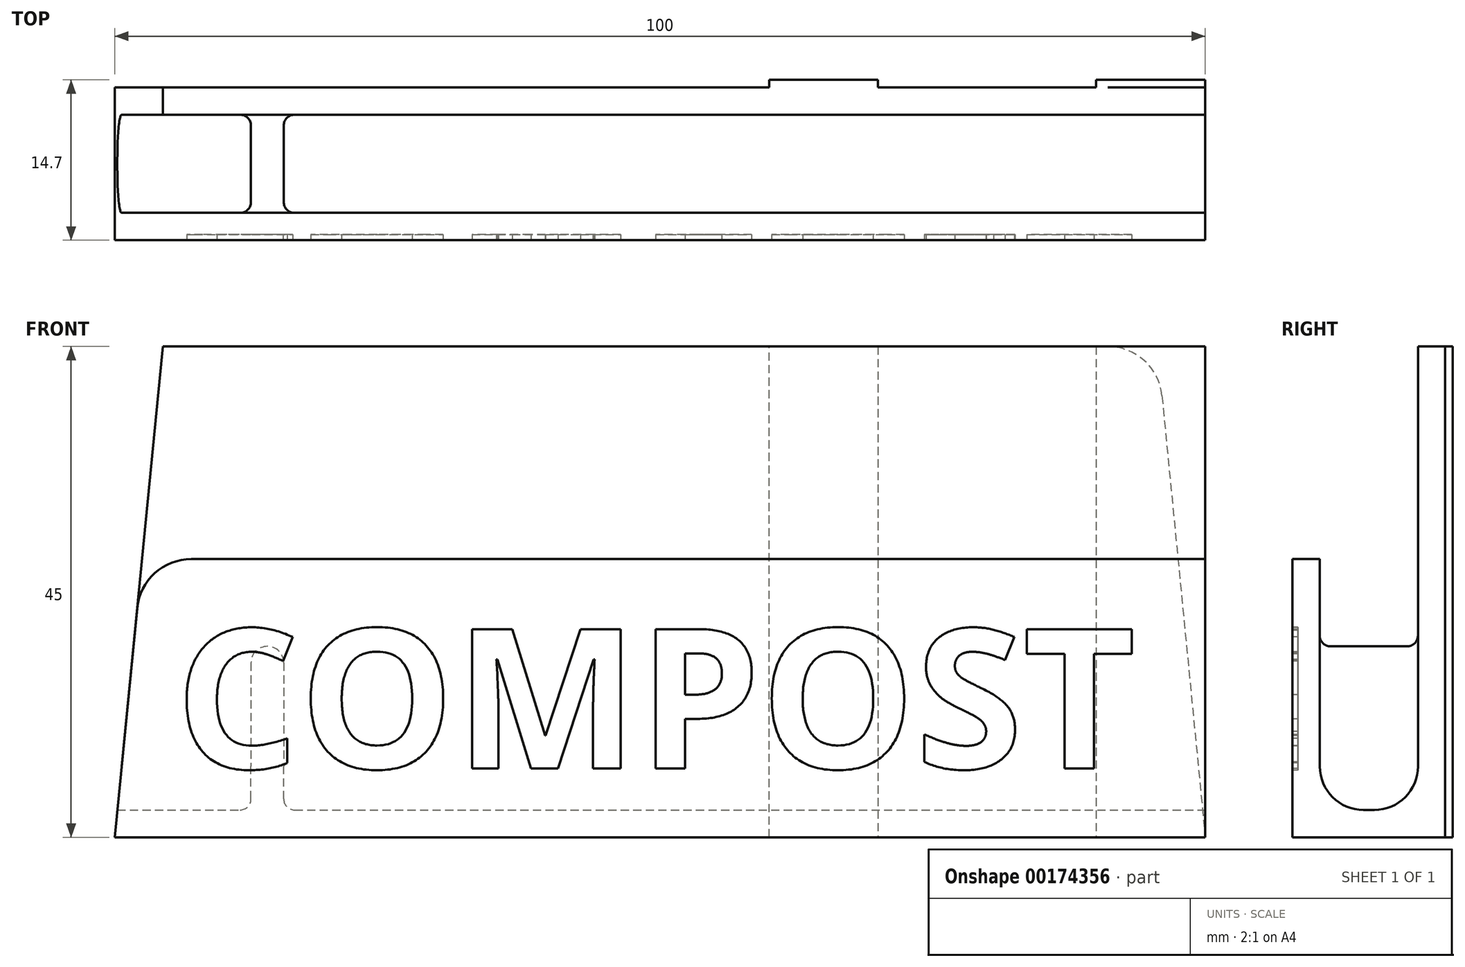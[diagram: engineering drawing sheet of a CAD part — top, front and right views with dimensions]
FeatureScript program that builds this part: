
annotation { "Feature Type Name" : "Feature", "Feature Type Description" : "" }
export const myFeature = defineFeature(function(context is Context, id is Id, definition is map)
    precondition{}
    {
        {
            var Q0;
            Q0=qCreatedBy(makeId("Top.planeOp"),FACE);
            var sketch = newSketch(context, id + "F0", { "sketchPlane" : qUnion([Q0])});
            skLineSegment(sketch, "E0.bottom", {"start": v(-50, 0) * mm, "end": v(50, 0) * mm});
            skLineSegment(sketch, "E0.top", {"start": v(-50, -14) * mm, "end": v(50, -14) * mm});
            skLineSegment(sketch, "E0.left", {"start": v(-50, 0) * mm, "end": v(-50, -14) * mm});
            skLineSegment(sketch, "E0.right", {"start": v(50, 0) * mm, "end": v(50, -14) * mm});
            skSolve(sketch);
        }
        {
            var Q0;
            Q0 = qSketchRegion(id + "F0", true);
            extrude(context, id + "F1", {"entities" : qUnion([Q0]), "depth" : 45 * mm});
        }
        {
            var Q0;
            Q0=makeQuery(id+"F1.opExtrude","CAP_FACE",FACE,{"disambiguationData":[OSD([sQuery(id+"F0.wireOp",EDGE,"E0.bottom"),sQuery(id+"F0.wireOp",EDGE,"E0.top"),sQuery(id+"F0.wireOp",EDGE,"E0.left"),sQuery(id+"F0.wireOp",EDGE,"E0.right")])],"isStart":false});
            var Q1;
            Q1=makeQuery(id+"F1.opExtrude","SWEPT_FACE",FACE,{"disambiguationData":[OSD([sQuery(id+"F0.wireOp",EDGE,"E0.left")])]});
            var Q2;
            Q2=makeQuery(id+"F1.opExtrude","SWEPT_FACE",FACE,{"disambiguationData":[OSD([sQuery(id+"F0.wireOp",EDGE,"E0.right")])]});
            shell(context, id + "F2", {"entities" : qUnion([Q0, Q1, Q2]), "thickness" : 2.5 * mm});
        }
        {
            var Q0;
            Q0=makeQuery(id+"F1.opExtrude","SWEPT_FACE",FACE,{"disambiguationData":[OSD([sQuery(id+"F0.wireOp",EDGE,"E0.top")])]});
            var sketch = newSketch(context, id + "F3", { "sketchPlane" : qUnion([Q0])});
            skLineSegment(sketch, "E1.bottom", {"start": v(-50, 45) * mm, "end": v(50, 45) * mm});
            skLineSegment(sketch, "E1.top", {"start": v(-50, 25.5) * mm, "end": v(50, 25.5) * mm});
            skLineSegment(sketch, "E1.left", {"start": v(-50, 45) * mm, "end": v(-50, 25.5) * mm});
            skLineSegment(sketch, "E1.right", {"start": v(50, 45) * mm, "end": v(50, 25.5) * mm});
            skLineSegment(sketch, "E2.0", {"start": v(-50, 2.5) * mm, "end": v(50, 2.5) * mm, "construction": true});
            skSolve(sketch);
        }
        {
            var Q0;
            Q0 = qSketchRegion(id + "F3", true);
            extrude(context, id + "F4", {"entities" : qUnion([Q0]), "operationType" : NewBodyOperationType.REMOVE, "endBound" : BoundingType.UP_TO_NEXT, "oppositeDirection" : true, "depth" : 25 * mm});
        }
        {
            var Q0;
            Q0=qCreatedBy(makeId("Front.planeOp"),FACE);
            var sketch = newSketch(context, id + "F5", { "sketchPlane" : qUnion([Q0])});
            skLineSegment(sketch, "E3", {"start": v(-45.59, 45) * mm, "end": v(-50, 0) * mm});
            skLineSegment(sketch, "E4", {"start": v(-50, 0) * mm, "end": v(-50, 45) * mm});
            skLineSegment(sketch, "E5", {"start": v(-50, 45) * mm, "end": v(-45.59, 45) * mm});
            skLineSegment(sketch, "E6", {"start": v(0, 0) * mm, "end": v(0, 36.7) * mm, "construction": true});
            skPoint(sketch, "E7", {"position": v(-47.5, 25.5) * mm});
            skSolve(sketch);
        }
        {
            var Q0;
            Q0 = qSketchRegion(id + "F5", true);
            extrude(context, id + "F6", {"entities" : qUnion([Q0]), "operationType" : NewBodyOperationType.REMOVE, "endBound" : BoundingType.THROUGH_ALL, "depth" : 25 * mm});
        }
        {
            var Q0;
            Q0=qCreatedBy(makeId("Front.planeOp"),FACE);
            var sketch = newSketch(context, id + "F7", { "sketchPlane" : qUnion([Q0])});
            skLineSegment(sketch, "E8.0", {"start": v(-55.05, 2.5) * mm, "end": v(50, 2.5) * mm, "construction": true});
            skLineSegment(sketch, "E9", {"start": v(-37.5, 2.5) * mm, "end": v(-37.5, 16) * mm});
            skArc(sketch, "E10", {"start": v(-34.5, 16) * mm, "mid": v(-36, 17.5) * mm, "end": v(-37.5, 16) * mm});
            skLineSegment(sketch, "E11", {"start": v(-34.5, 16) * mm, "end": v(-34.5, 2.5) * mm});
            skLineSegment(sketch, "E12", {"start": v(-36, 17.5) * mm, "end": v(-31.62, 17.5) * mm, "construction": true});
            skLineSegment(sketch, "E13", {"start": v(0, 0) * mm, "end": v(0, 34.62) * mm, "construction": true});
            skLineSegment(sketch, "E14", {"start": v(-37.5, 2.5) * mm, "end": v(-34.5, 2.5) * mm});
            skSolve(sketch);
        }
        {
            var Q0;
            Q0 = qSketchRegion(id + "F7", true);
            var Q1;
            Q1=makeQuery(id+"F2.opShell","OFFSET_FACE",FACE,{"disambiguationData":[OSD([sQuery(id+"F0.wireOp",EDGE,"E0.top")])]});
            extrude(context, id + "F8", {"entities" : qUnion([Q0]), "operationType" : NewBodyOperationType.ADD, "endBound" : BoundingType.UP_TO_SURFACE, "endBoundEntityFace" : qUnion([Q1]), "depth" : 25 * mm});
        }
        {
            var Q0;
            {var subQ0=sQuery(id+"F0.wireOp",EDGE,"E0.bottom");var subQ2=sQuery(id+"F0.wireOp",EDGE,"E0.right");var subQ6=sQuery(id+"F7.wireOp",EDGE,"E11");var subQ7=makeQuery(id+"F8.opExtrude","SWEPT_FACE",FACE,{"disambiguationData":[OSD([subQ6])]});Q0=makeQuery(id+"F897hcUD9pJ6nv1_1.1.F8.boolean.opBoolean","SPLIT",EDGE,{"disambiguationData":[TD([subQ7])],"derivedFrom":makeQuery(id+"F8.boolean.opBoolean","SPLIT",EDGE,{"disambiguationData":[TD([makeQuery(id+"F1.opExtrude","SWEPT_FACE",FACE,{"disambiguationData":[OSD([subQ2])]})])],"derivedFrom":makeQuery(id+"F2.opShell","OFFSET_EDGE",EDGE,{"disambiguationData":[OSD([subQ0]),TDD([makeQuery(id+"F1.opExtrude","CAP_EDGE",EDGE,{"disambiguationData":[OSD([subQ0])],"isStart":true})])]})})});}
            var Q1;
            {var subQ0=sQuery(id+"F0.wireOp",EDGE,"E0.left");var subQ1=sQuery(id+"F0.wireOp",EDGE,"E0.bottom");Q1=makeQuery(id+"F8.boolean.opBoolean","SPLIT",EDGE,{"disambiguationData":[TD([makeQuery(id+"F1.opExtrude","SWEPT_FACE",FACE,{"disambiguationData":[OSD([subQ0])]})])],"derivedFrom":makeQuery(id+"F2.opShell","OFFSET_EDGE",EDGE,{"disambiguationData":[OSD([subQ1]),TDD([makeQuery(id+"F1.opExtrude","CAP_EDGE",EDGE,{"disambiguationData":[OSD([subQ1])],"isStart":true})])]})});}
            var Q2;
            {var subQ0=sQuery(id+"F0.wireOp",EDGE,"E0.right");var subQ1=makeQuery(id+"F1.opExtrude","SWEPT_FACE",FACE,{"disambiguationData":[OSD([subQ0])]});var subQ2=sQuery(id+"F0.wireOp",EDGE,"E0.bottom");Q2=makeQuery(id+"F897hcUD9pJ6nv1_1.1.F8.boolean.opBoolean","SPLIT",EDGE,{"disambiguationData":[TD([subQ1])],"derivedFrom":makeQuery(id+"F8.boolean.opBoolean","SPLIT",EDGE,{"disambiguationData":[TD([subQ1])],"derivedFrom":makeQuery(id+"F2.opShell","OFFSET_EDGE",EDGE,{"disambiguationData":[OSD([subQ2]),TDD([makeQuery(id+"F1.opExtrude","CAP_EDGE",EDGE,{"disambiguationData":[OSD([subQ2])],"isStart":true})])]})})});}
            var Q3;
            {var subQ0=sQuery(id+"F0.wireOp",EDGE,"E0.right");var subQ1=makeQuery(id+"F1.opExtrude","SWEPT_FACE",FACE,{"disambiguationData":[OSD([subQ0])]});var subQ3=sQuery(id+"F0.wireOp",EDGE,"E0.top");Q3=makeQuery(id+"F897hcUD9pJ6nv1_1.1.F8.boolean.opBoolean","SPLIT",EDGE,{"disambiguationData":[TD([subQ1])],"derivedFrom":makeQuery(id+"F8.boolean.opBoolean","SPLIT",EDGE,{"disambiguationData":[TD([subQ1])],"derivedFrom":makeQuery(id+"F2.opShell","OFFSET_EDGE",EDGE,{"disambiguationData":[OSD([subQ3]),TDD([makeQuery(id+"F1.opExtrude","CAP_EDGE",EDGE,{"disambiguationData":[OSD([subQ3])],"isStart":true})])]})})});}
            var Q4;
            {var subQ0=sQuery(id+"F0.wireOp",EDGE,"E0.right");var subQ2=sQuery(id+"F0.wireOp",EDGE,"E0.top");var subQ5=sQuery(id+"F7.wireOp",EDGE,"E11");var subQ7=makeQuery(id+"F8.opExtrude","SWEPT_FACE",FACE,{"disambiguationData":[OSD([subQ5])]});Q4=makeQuery(id+"F897hcUD9pJ6nv1_1.1.F8.boolean.opBoolean","SPLIT",EDGE,{"disambiguationData":[TD([subQ7])],"derivedFrom":makeQuery(id+"F8.boolean.opBoolean","SPLIT",EDGE,{"disambiguationData":[TD([makeQuery(id+"F1.opExtrude","SWEPT_FACE",FACE,{"disambiguationData":[OSD([subQ0])]})])],"derivedFrom":makeQuery(id+"F2.opShell","OFFSET_EDGE",EDGE,{"disambiguationData":[OSD([subQ2]),TDD([makeQuery(id+"F1.opExtrude","CAP_EDGE",EDGE,{"disambiguationData":[OSD([subQ2])],"isStart":true})])]})})});}
            var Q5;
            {var subQ0=sQuery(id+"F0.wireOp",EDGE,"E0.left");var subQ2=sQuery(id+"F0.wireOp",EDGE,"E0.top");Q5=makeQuery(id+"F8.boolean.opBoolean","SPLIT",EDGE,{"disambiguationData":[TD([makeQuery(id+"F1.opExtrude","SWEPT_FACE",FACE,{"disambiguationData":[OSD([subQ0])]})])],"derivedFrom":makeQuery(id+"F2.opShell","OFFSET_EDGE",EDGE,{"disambiguationData":[OSD([subQ2]),TDD([makeQuery(id+"F1.opExtrude","CAP_EDGE",EDGE,{"disambiguationData":[OSD([subQ2])],"isStart":true})])]})});}
            var Q6;
            {var subQ0=sQuery(id+"F0.wireOp",EDGE,"E0.bottom");Q6=makeQuery(id+"F8.boolean.opBoolean","SPLIT",EDGE,{"disambiguationData":[TD([makeQuery(id+"F6.boolean.opBoolean","COPY",FACE,{"derivedFrom":makeQuery(id+"F6.opExtrude","SWEPT_FACE",FACE,{"disambiguationData":[OSD([sQuery(id+"F5.wireOp",EDGE,"E3")])]})})])],"derivedFrom":makeQuery(id+"F2.opShell","OFFSET_EDGE",EDGE,{"disambiguationData":[OSD([subQ0]),TDD([makeQuery(id+"F1.opExtrude","CAP_EDGE",EDGE,{"disambiguationData":[OSD([subQ0])],"isStart":true})])]})});}
            var Q7;
            {var subQ2=sQuery(id+"F0.wireOp",EDGE,"E0.top");Q7=makeQuery(id+"F8.boolean.opBoolean","SPLIT",EDGE,{"disambiguationData":[TD([makeQuery(id+"F6.boolean.opBoolean","COPY",FACE,{"derivedFrom":makeQuery(id+"F6.opExtrude","SWEPT_FACE",FACE,{"disambiguationData":[OSD([sQuery(id+"F5.wireOp",EDGE,"E3")])]})})])],"derivedFrom":makeQuery(id+"F2.opShell","OFFSET_EDGE",EDGE,{"disambiguationData":[OSD([subQ2]),TDD([makeQuery(id+"F1.opExtrude","CAP_EDGE",EDGE,{"disambiguationData":[OSD([subQ2])],"isStart":true})])]})});}
            var Q8;
            {var subQ0=sQuery(id+"F0.wireOp",EDGE,"E0.bottom");var subQ2=sQuery(id+"F0.wireOp",EDGE,"E0.right");Q8=makeQuery(id+"F897hcUD9pJ6nv1_1.1.F8.boolean.opBoolean","SPLIT",EDGE,{"disambiguationData":[TD([makeQuery(id+"F897hcUD9pJ6nv1_1.1.F6.boolean.opBoolean","COPY",FACE,{"derivedFrom":makeQuery(id+"F897hcUD9pJ6nv1_1.1.F6.opExtrude","SWEPT_FACE",FACE,{"disambiguationData":[OSD([sQuery(id+"F5.wireOp",EDGE,"E3")])]})})])],"derivedFrom":makeQuery(id+"F8.boolean.opBoolean","SPLIT",EDGE,{"disambiguationData":[TD([makeQuery(id+"F1.opExtrude","SWEPT_FACE",FACE,{"disambiguationData":[OSD([subQ2])]})])],"derivedFrom":makeQuery(id+"F2.opShell","OFFSET_EDGE",EDGE,{"disambiguationData":[OSD([subQ0]),TDD([makeQuery(id+"F1.opExtrude","CAP_EDGE",EDGE,{"disambiguationData":[OSD([subQ0])],"isStart":true})])]})})});}
            var Q9;
            {var subQ0=sQuery(id+"F0.wireOp",EDGE,"E0.right");var subQ2=sQuery(id+"F0.wireOp",EDGE,"E0.top");Q9=makeQuery(id+"F897hcUD9pJ6nv1_1.1.F8.boolean.opBoolean","SPLIT",EDGE,{"disambiguationData":[TD([makeQuery(id+"F897hcUD9pJ6nv1_1.1.F6.boolean.opBoolean","COPY",FACE,{"derivedFrom":makeQuery(id+"F897hcUD9pJ6nv1_1.1.F6.opExtrude","SWEPT_FACE",FACE,{"disambiguationData":[OSD([sQuery(id+"F5.wireOp",EDGE,"E3")])]})})])],"derivedFrom":makeQuery(id+"F8.boolean.opBoolean","SPLIT",EDGE,{"disambiguationData":[TD([makeQuery(id+"F1.opExtrude","SWEPT_FACE",FACE,{"disambiguationData":[OSD([subQ0])]})])],"derivedFrom":makeQuery(id+"F2.opShell","OFFSET_EDGE",EDGE,{"disambiguationData":[OSD([subQ2]),TDD([makeQuery(id+"F1.opExtrude","CAP_EDGE",EDGE,{"disambiguationData":[OSD([subQ2])],"isStart":true})])]})})});}
            fillet(context, id + "F9", {"entities" : qUnion([Q0, Q1, Q2, Q3, Q4, Q5, Q6, Q7, Q8, Q9]), "radius" : 4 * mm, "tangentPropagation" : true, "allowEdgeOverflow" : false});
        }
        {
            var Q0;
            Q0=makeQuery(id+"F8.boolean.opBoolean","INTERSECT",EDGE,{"derivedFrom":[makeQuery(id+"F2.opShell","OFFSET_FACE",FACE,{"disambiguationData":[OSD([sQuery(id+"F0.wireOp",EDGE,"E0.bottom")])]}),makeQuery(id+"F8.opExtrude","SWEPT_FACE",FACE,{"disambiguationData":[OSD([sQuery(id+"F7.wireOp",EDGE,"E10")])]})]});
            var Q1;
            Q1=makeQuery(id+"F897hcUD9pJ6nv1_1.1.F8.boolean.opBoolean","INTERSECT",EDGE,{"derivedFrom":[makeQuery(id+"F2.opShell","OFFSET_FACE",FACE,{"disambiguationData":[OSD([sQuery(id+"F0.wireOp",EDGE,"E0.bottom")])]}),makeQuery(id+"F897hcUD9pJ6nv1_1.1.F8.opExtrude","SWEPT_FACE",FACE,{"disambiguationData":[OSD([sQuery(id+"F7.wireOp",EDGE,"E10")])]})]});
            fillet(context, id + "F10", {"entities" : qUnion([Q0, Q1]), "radius" : 1 * mm, "tangentPropagation" : true, "allowEdgeOverflow" : false});
        }
        {
            var Q0;
            Q0=makeQuery(id+"F6.boolean.opBoolean","COPY",EDGE,{"derivedFrom":makeQuery(id+"F6.opExtrude","SWEPT_EDGE",EDGE,{"disambiguationData":[OSD([sQuery(id+"F5.wireOp",EDGE,"E3"),sQuery(id+"F5.wireOp",EDGE,"E5")])]})});
            var Q1;
            Q1=makeQuery(id+"F897hcUD9pJ6nv1_1.1.F6.boolean.opBoolean","COPY",EDGE,{"derivedFrom":makeQuery(id+"F897hcUD9pJ6nv1_1.1.F6.opExtrude","SWEPT_EDGE",EDGE,{"disambiguationData":[OSD([sQuery(id+"F5.wireOp",EDGE,"E3"),sQuery(id+"F5.wireOp",EDGE,"E5")])]})});
            var Q2;
            Q2=makeQuery(id+"F897hcUD9pJ6nv1_1.1.F6.boolean.opBoolean","INTERSECT",EDGE,{"derivedFrom":[makeQuery(id+"F4.boolean.opBoolean","COPY",FACE,{"derivedFrom":makeQuery(id+"F4.opExtrude","SWEPT_FACE",FACE,{"disambiguationData":[OSD([sQuery(id+"F3.wireOp",EDGE,"E1.top")])]})}),makeQuery(id+"F897hcUD9pJ6nv1_1.1.F6.opExtrude","SWEPT_FACE",FACE,{"disambiguationData":[OSD([sQuery(id+"F5.wireOp",EDGE,"E3")])]})]});
            var Q3;
            Q3=makeQuery(id+"F6.boolean.opBoolean","INTERSECT",EDGE,{"derivedFrom":[makeQuery(id+"F4.boolean.opBoolean","COPY",FACE,{"derivedFrom":makeQuery(id+"F4.opExtrude","SWEPT_FACE",FACE,{"disambiguationData":[OSD([sQuery(id+"F3.wireOp",EDGE,"E1.top")])]})}),makeQuery(id+"F6.opExtrude","SWEPT_FACE",FACE,{"disambiguationData":[OSD([sQuery(id+"F5.wireOp",EDGE,"E3")])]})]});
            fillet(context, id + "F11", {"entities" : qUnion([Q0, Q1, Q2, Q3]), "radius" : 5 * mm, "tangentPropagation" : true, "allowEdgeOverflow" : false});
        }
        {
            var Q0;
            Q0=qCreatedBy(makeId("Front.planeOp"),FACE);
            var sketch = newSketch(context, id + "F12", { "sketchPlane" : qUnion([Q0])});
            skLineSegment(sketch, "E15.0", {"start": v(10, 45) * mm, "end": v(20, 45) * mm});
            skArc(sketch, "E16.0", {"start": v(41.05, 45) * mm, "mid": v(44.41, 43.7) * mm, "end": v(46.03, 40.49) * mm});
            skLineSegment(sketch, "E16.1", {"start": v(46.03, 40.49) * mm, "end": v(50, 0) * mm});
            skLineSegment(sketch, "E16.2", {"start": v(10, 0) * mm, "end": v(20, 0) * mm});
            skPoint(sketch, "E16.4.start.orphan", {"position": v(-46.03, 40.49) * mm});
            skPoint(sketch, "E17.orphan", {"position": v(-41.05, 45) * mm});
            skPoint(sketch, "E18.orphan", {"position": v(-50, 0) * mm});
            skLineSegment(sketch, "E19.left", {"start": v(40, 45) * mm, "end": v(40, 0) * mm});
            skLineSegment(sketch, "E19.right", {"start": v(20, 45) * mm, "end": v(20, 0) * mm});
            skLineSegment(sketch, "E20.trimOffspring", {"start": v(40, 45) * mm, "end": v(41.05, 45) * mm});
            skLineSegment(sketch, "E21.trimOffspring", {"start": v(40, 0) * mm, "end": v(50, 0) * mm});
            skLineSegment(sketch, "E22", {"start": v(10, 0) * mm, "end": v(10, 45) * mm});
            skLineSegment(sketch, "E23", {"start": v(0, 0) * mm, "end": v(0, 52.27) * mm, "construction": true});
            skSolve(sketch);
        }
        {
            var Q0;
            Q0 = qSketchRegion(id + "F12", true);
            extrude(context, id + "F13", {"entities" : qUnion([Q0]), "operationType" : NewBodyOperationType.ADD, "oppositeDirection" : true, "depth" : .7 * mm});
        }
        {
            var Q0;
            Q0=makeQuery(id+"F1.opExtrude","SWEPT_FACE",FACE,{"disambiguationData":[OSD([sQuery(id+"F0.wireOp",EDGE,"E0.top")])]});
            var sketch = newSketch(context, id + "F14", { "sketchPlane" : qUnion([Q0])});
            skText(sketch, "E24", { "text": "COMPOST", "fontName": "OpenSans-Bold.ttf"});
            skLineSegment(sketch, "E25", {"start": v(0, 0) * mm, "end": v(0, 6.32) * mm, "construction": true});
            skLineSegment(sketch, "E26", {"start": v(0, 19.18) * mm, "end": v(0, 25.5) * mm, "construction": true});
            const initialGuessF14  = {"E24": [-0.04444, 0.00632, 1, 0, 0.01286]};
            skSetInitialGuess(sketch, initialGuessF14);
            skSolve(sketch);
        }
        {
            var Q0;
            Q0 = qSketchRegion(id + "F14", true);
            extrude(context, id + "F15", {"entities" : qUnion([Q0]), "operationType" : NewBodyOperationType.REMOVE, "oppositeDirection" : true, "depth" : .5 * mm});
        }
    });
